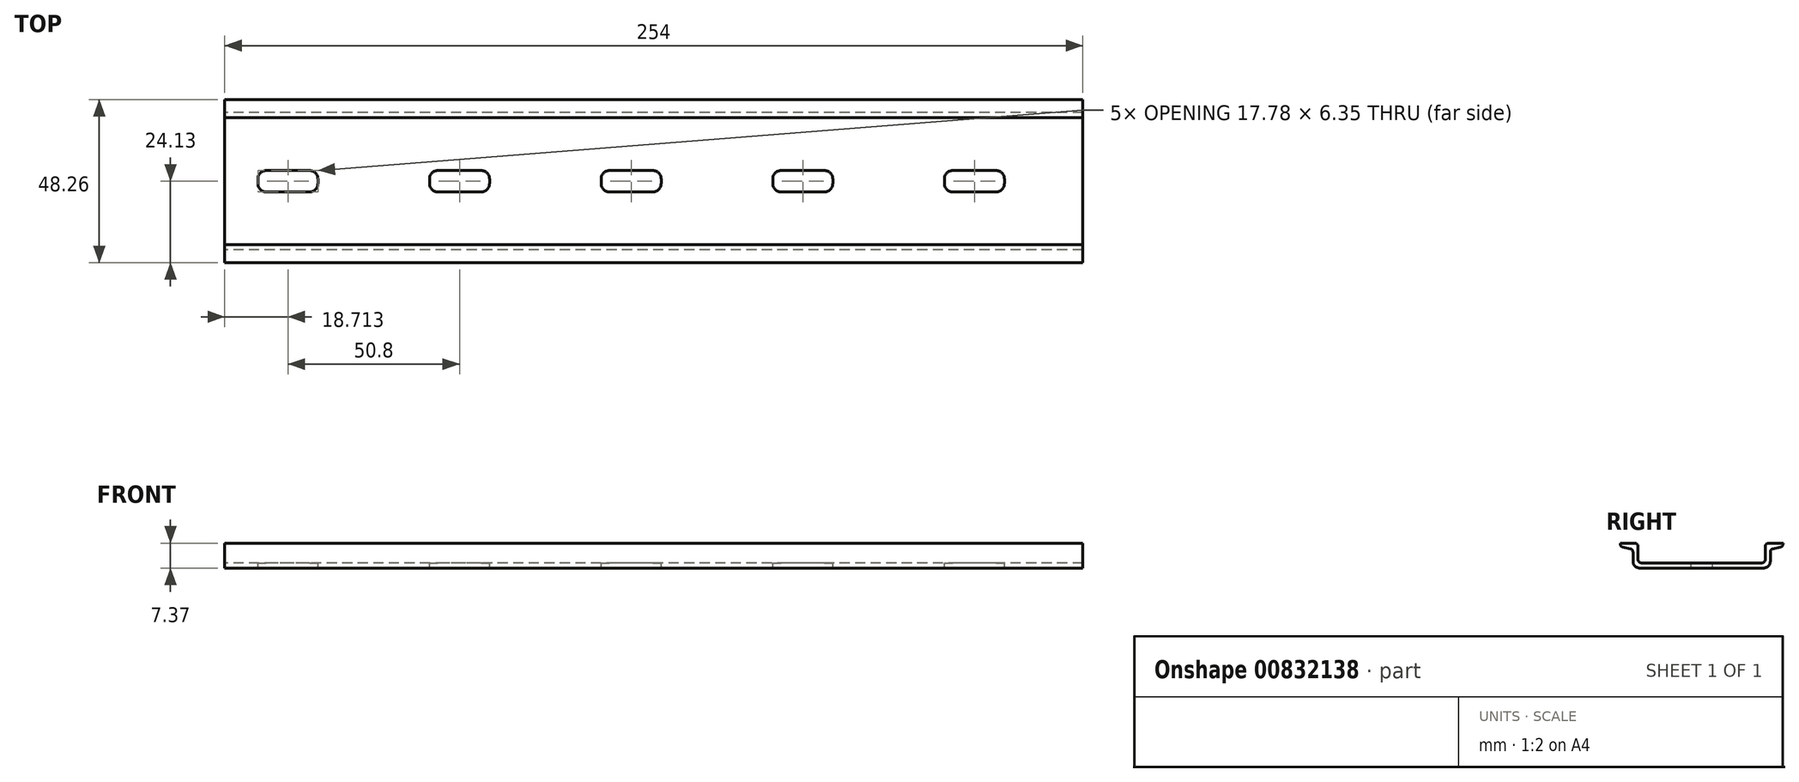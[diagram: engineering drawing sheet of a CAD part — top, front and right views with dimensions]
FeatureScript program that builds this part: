
annotation { "Feature Type Name" : "Feature", "Feature Type Description" : "" }
export const myFeature = defineFeature(function(context is Context, id is Id, definition is map)
    precondition{}
    {
        {
            var Q0;
            Q0=qCreatedBy(makeId("Right.planeOp"),FACE);
            var sketch = newSketch(context, id + "F0", { "sketchPlane" : qUnion([Q0])});
            skLineSegment(sketch, "E0", {"start": v(2, 0) * mm, "end": v(38.76, 0) * mm});
            skLineSegment(sketch, "E1", {"start": v(0, 7.37) * mm, "end": v(-3.81, 7.37) * mm});
            skLineSegment(sketch, "E2", {"start": v(40.64, 7.37) * mm, "end": v(44.45, 7.37) * mm});
            skPoint(sketch, "E3.visualSharp", {"position": v(40.64, 0) * mm});
            skPoint(sketch, "E4.visualSharp", {"position": v(0, 0) * mm});
            skArc(sketch, "E4.filletArc", {"start": v(0, 2) * mm, "mid": v(0.59, 0.59) * mm, "end": v(2, 0) * mm});
            skLineSegment(sketch, "E5.0", {"start": v(1.5, 2.5) * mm, "end": v(1.5, 7.37) * mm});
            skLineSegment(sketch, "E5.1", {"start": v(2.5, 1.5) * mm, "end": v(38.14, 1.5) * mm});
            skLineSegment(sketch, "E5.2", {"start": v(39.14, 2.5) * mm, "end": v(39.14, 7.37) * mm});
            skPoint(sketch, "E6.visualSharp", {"position": v(39.14, 1.5) * mm});
            skArc(sketch, "E6.filletArc", {"start": v(38.14, 1.5) * mm, "mid": v(38.85, 1.8) * mm, "end": v(39.14, 2.5) * mm});
            skPoint(sketch, "E7.visualSharp", {"position": v(1.5, 1.5) * mm});
            skArc(sketch, "E7.filletArc", {"start": v(1.5, 2.5) * mm, "mid": v(1.8, 1.8) * mm, "end": v(2.5, 1.5) * mm});
            skLineSegment(sketch, "E8", {"start": v(44.45, 7.37) * mm, "end": v(44.45, 6.37) * mm});
            skLineSegment(sketch, "E9", {"start": v(40.64, 7.37) * mm, "end": v(39.14, 7.37) * mm});
            skLineSegment(sketch, "E10", {"start": v(-3.81, 7.37) * mm, "end": v(-3.81, 6.37) * mm});
            skLineSegment(sketch, "E11", {"start": v(0, 7.37) * mm, "end": v(1.5, 7.37) * mm});
            skLineSegment(sketch, "E12", {"start": v(0, 2) * mm, "end": v(0, 5.56) * mm});
            skLineSegment(sketch, "E13", {"start": v(-3.81, 6.37) * mm, "end": v(0, 5.56) * mm});
            skLineSegment(sketch, "E14", {"start": v(38.64, 0) * mm, "end": v(38.76, 0) * mm});
            skArc(sketch, "E15.filletArc", {"start": v(38.64, 0) * mm, "mid": v(40.05, 0.59) * mm, "end": v(40.64, 2) * mm});
            skLineSegment(sketch, "E16", {"start": v(40.64, 2) * mm, "end": v(40.64, 5.56) * mm});
            skLineSegment(sketch, "E17", {"start": v(40.64, 5.56) * mm, "end": v(44.45, 6.37) * mm});
            skSolve(sketch);
        }
        {
            var Q0;
            Q0 = qSketchRegion(id + "F0", true);
            extrude(context, id + "F1", {"entities" : qUnion([Q0]), "depth" : 254 * mm, "offsetDistance" : 25.4 * mm});
        }
        {
            var Q0;
            Q0=makeQuery(id+"F1.opExtrude","SWEPT_EDGE",EDGE,{"disambiguationData":[OSD([sQuery(id+"F0.wireOp",EDGE,"E5.2"),sQuery(id+"F0.wireOp",EDGE,"E9")])]});
            var Q1;
            Q1=makeQuery(id+"F1.opExtrude","SWEPT_EDGE",EDGE,{"disambiguationData":[OSD([sQuery(id+"F0.wireOp",EDGE,"E5.0"),sQuery(id+"F0.wireOp",EDGE,"E11")])]});
            var Q2;
            Q2=makeQuery(id+"F1.opExtrude","SWEPT_EDGE",EDGE,{"disambiguationData":[OSD([sQuery(id+"F0.wireOp",EDGE,"E12"),sQuery(id+"F0.wireOp",EDGE,"E13")])]});
            var Q3;
            Q3=makeQuery(id+"F1.opExtrude","SWEPT_EDGE",EDGE,{"disambiguationData":[OSD([sQuery(id+"F0.wireOp",EDGE,"E16"),sQuery(id+"F0.wireOp",EDGE,"E17")])]});
            var Q4;
            Q4=makeQuery(id+"F1.opExtrude","SWEPT_EDGE",EDGE,{"disambiguationData":[OSD([sQuery(id+"F0.wireOp",EDGE,"E8"),sQuery(id+"F0.wireOp",EDGE,"E17")])]});
            var Q5;
            Q5=makeQuery(id+"F1.opExtrude","SWEPT_EDGE",EDGE,{"disambiguationData":[OSD([sQuery(id+"F0.wireOp",EDGE,"E10"),sQuery(id+"F0.wireOp",EDGE,"E13")])]});
            fillet(context, id + "F2", {"entities" : qUnion([Q0, Q1, Q2, Q3, Q4, Q5]), "radius" : 1 * mm, "tangentPropagation" : true, "allowEdgeOverflow" : false});
        }
        {
            var Q0;
            Q0=makeQuery(id+"F1.opExtrude","SWEPT_FACE",FACE,{"disambiguationData":[OSD([sQuery(id+"F0.wireOp",EDGE,"E5.1")])]});
            var sketch = newSketch(context, id + "F3", { "sketchPlane" : qUnion([Q0])});
            skLineSegment(sketch, "E18.bottom", {"start": v(25.1, 17.15) * mm, "end": v(12.32, 17.15) * mm});
            skLineSegment(sketch, "E18.top", {"start": v(25.1, 23.5) * mm, "end": v(12.32, 23.5) * mm});
            skLineSegment(sketch, "E18.left", {"start": v(27.6, 19.65) * mm, "end": v(27.6, 21) * mm});
            skLineSegment(sketch, "E18.right", {"start": v(9.82, 19.65) * mm, "end": v(9.82, 21) * mm});
            skPoint(sketch, "E18.middle", {"position": v(18.71, 20.32) * mm});
            skPoint(sketch, "E19.visualSharp", {"position": v(27.6, 23.5) * mm});
            skArc(sketch, "E19.filletArc", {"start": v(27.6, 21) * mm, "mid": v(26.87, 22.76) * mm, "end": v(25.1, 23.5) * mm});
            skPoint(sketch, "E20.visualSharp", {"position": v(27.6, 17.15) * mm});
            skArc(sketch, "E20.filletArc", {"start": v(25.1, 17.15) * mm, "mid": v(26.87, 17.88) * mm, "end": v(27.6, 19.65) * mm});
            skPoint(sketch, "E21.visualSharp", {"position": v(9.82, 23.5) * mm});
            skArc(sketch, "E21.filletArc", {"start": v(12.32, 23.5) * mm, "mid": v(10.56, 22.76) * mm, "end": v(9.82, 21) * mm});
            skPoint(sketch, "E22.visualSharp", {"position": v(9.82, 17.15) * mm});
            skArc(sketch, "E22.filletArc", {"start": v(9.82, 19.65) * mm, "mid": v(10.56, 17.88) * mm, "end": v(12.32, 17.15) * mm});
            skLineSegment(sketch, "E23.1.0.0", {"start": v(75.9, 23.5) * mm, "end": v(63.12, 23.5) * mm});
            skLineSegment(sketch, "E23.1.0.1", {"start": v(75.9, 17.15) * mm, "end": v(63.12, 17.15) * mm});
            skArc(sketch, "E23.1.0.2", {"start": v(75.9, 17.15) * mm, "mid": v(77.67, 17.88) * mm, "end": v(78.4, 19.65) * mm});
            skLineSegment(sketch, "E23.1.0.3", {"start": v(78.4, 19.65) * mm, "end": v(78.4, 21) * mm});
            skArc(sketch, "E23.1.0.4", {"start": v(78.4, 21) * mm, "mid": v(77.67, 22.76) * mm, "end": v(75.9, 23.5) * mm});
            skArc(sketch, "E23.1.0.5", {"start": v(63.12, 23.5) * mm, "mid": v(61.36, 22.76) * mm, "end": v(60.62, 21) * mm});
            skLineSegment(sketch, "E23.1.0.6", {"start": v(60.62, 19.65) * mm, "end": v(60.62, 21) * mm});
            skArc(sketch, "E23.1.0.7", {"start": v(60.62, 19.65) * mm, "mid": v(61.36, 17.88) * mm, "end": v(63.12, 17.15) * mm});
            skLineSegment(sketch, "E23.2.0.0", {"start": v(126.7, 23.5) * mm, "end": v(113.92, 23.5) * mm});
            skLineSegment(sketch, "E23.2.0.1", {"start": v(126.7, 17.15) * mm, "end": v(113.92, 17.15) * mm});
            skArc(sketch, "E23.2.0.2", {"start": v(126.7, 17.15) * mm, "mid": v(128.47, 17.88) * mm, "end": v(129.2, 19.65) * mm});
            skLineSegment(sketch, "E23.2.0.3", {"start": v(129.2, 19.65) * mm, "end": v(129.2, 21) * mm});
            skArc(sketch, "E23.2.0.4", {"start": v(129.2, 21) * mm, "mid": v(128.47, 22.76) * mm, "end": v(126.7, 23.5) * mm});
            skArc(sketch, "E23.2.0.5", {"start": v(113.92, 23.5) * mm, "mid": v(112.16, 22.76) * mm, "end": v(111.42, 21) * mm});
            skLineSegment(sketch, "E23.2.0.6", {"start": v(111.42, 19.65) * mm, "end": v(111.42, 21) * mm});
            skArc(sketch, "E23.2.0.7", {"start": v(111.42, 19.65) * mm, "mid": v(112.16, 17.88) * mm, "end": v(113.92, 17.15) * mm});
            skLineSegment(sketch, "E23.3.0.0", {"start": v(177.5, 23.5) * mm, "end": v(164.72, 23.5) * mm});
            skLineSegment(sketch, "E23.3.0.1", {"start": v(177.5, 17.15) * mm, "end": v(164.72, 17.15) * mm});
            skArc(sketch, "E23.3.0.2", {"start": v(177.5, 17.15) * mm, "mid": v(179.27, 17.88) * mm, "end": v(180, 19.65) * mm});
            skLineSegment(sketch, "E23.3.0.3", {"start": v(180, 19.65) * mm, "end": v(180, 21) * mm});
            skArc(sketch, "E23.3.0.4", {"start": v(180, 21) * mm, "mid": v(179.27, 22.76) * mm, "end": v(177.5, 23.5) * mm});
            skArc(sketch, "E23.3.0.5", {"start": v(164.72, 23.5) * mm, "mid": v(162.96, 22.76) * mm, "end": v(162.22, 21) * mm});
            skLineSegment(sketch, "E23.3.0.6", {"start": v(162.22, 19.65) * mm, "end": v(162.22, 21) * mm});
            skArc(sketch, "E23.3.0.7", {"start": v(162.22, 19.65) * mm, "mid": v(162.96, 17.88) * mm, "end": v(164.72, 17.15) * mm});
            skLineSegment(sketch, "E23.4.0.0", {"start": v(228.3, 23.5) * mm, "end": v(215.52, 23.5) * mm});
            skLineSegment(sketch, "E23.4.0.1", {"start": v(228.3, 17.15) * mm, "end": v(215.52, 17.15) * mm});
            skArc(sketch, "E23.4.0.2", {"start": v(228.3, 17.15) * mm, "mid": v(230.07, 17.88) * mm, "end": v(230.8, 19.65) * mm});
            skLineSegment(sketch, "E23.4.0.3", {"start": v(230.8, 19.65) * mm, "end": v(230.8, 21) * mm});
            skArc(sketch, "E23.4.0.4", {"start": v(230.8, 21) * mm, "mid": v(230.07, 22.76) * mm, "end": v(228.3, 23.5) * mm});
            skArc(sketch, "E23.4.0.5", {"start": v(215.52, 23.5) * mm, "mid": v(213.76, 22.76) * mm, "end": v(213.02, 21) * mm});
            skLineSegment(sketch, "E23.4.0.6", {"start": v(213.02, 19.65) * mm, "end": v(213.02, 21) * mm});
            skArc(sketch, "E23.4.0.7", {"start": v(213.02, 19.65) * mm, "mid": v(213.76, 17.88) * mm, "end": v(215.52, 17.15) * mm});
            skSolve(sketch);
        }
        {
            var Q0;
            Q0 = qSketchRegion(id + "F3", true);
            extrude(context, id + "F4", {"entities" : qUnion([Q0]), "operationType" : NewBodyOperationType.REMOVE, "oppositeDirection" : true, "depth" : 25.4 * mm, "offsetDistance" : 25.4 * mm});
        }
    });
